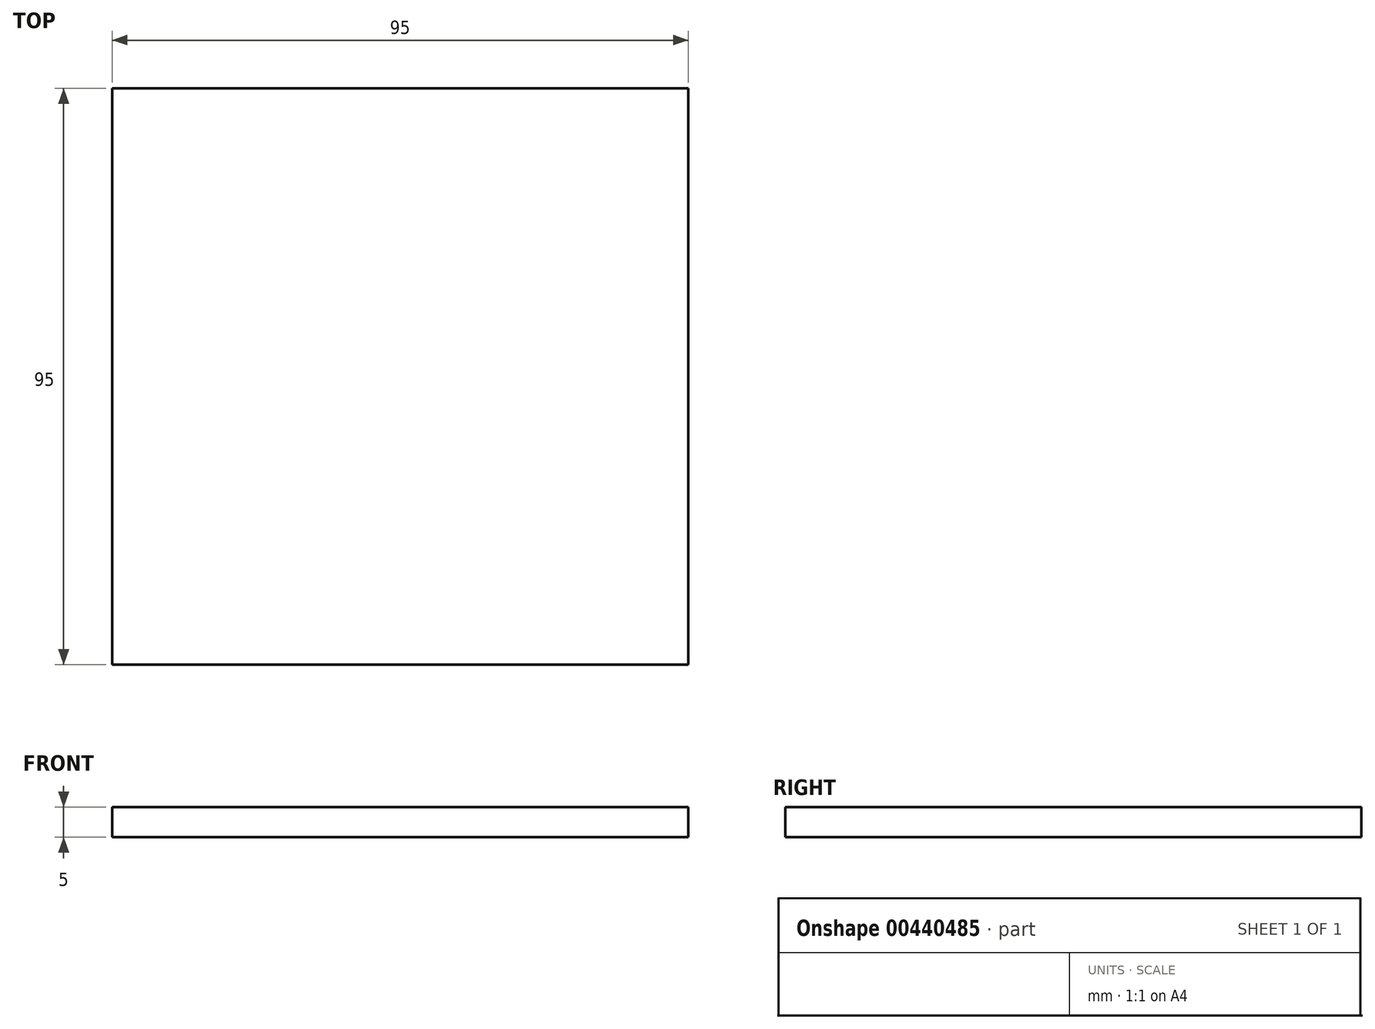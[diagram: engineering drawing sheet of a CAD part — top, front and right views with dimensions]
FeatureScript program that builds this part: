
annotation { "Feature Type Name" : "Feature", "Feature Type Description" : "" }
export const myFeature = defineFeature(function(context is Context, id is Id, definition is map)
    precondition{}
    {
        {
            var Q0;
            Q0=qCreatedBy(makeId("Top.planeOp"),FACE);
            var sketch = newSketch(context, id + "F0", { "sketchPlane" : qUnion([Q0])});
            skLineSegment(sketch, "E0.bottom", {"start": v(-47.5, -47.5) * mm, "end": v(47.5, -47.5) * mm});
            skLineSegment(sketch, "E0.top", {"start": v(-47.5, 47.5) * mm, "end": v(47.5, 47.5) * mm});
            skLineSegment(sketch, "E0.left", {"start": v(-47.5, -47.5) * mm, "end": v(-47.5, 47.5) * mm});
            skLineSegment(sketch, "E0.right", {"start": v(47.5, -47.5) * mm, "end": v(47.5, 47.5) * mm});
            skPoint(sketch, "E0.middle", {"position": v(0, 0) * mm});
            skSolve(sketch);
        }
        {
            var Q0;
            Q0 = qSketchRegion(id + "F0", true);
            extrude(context, id + "F1", {"entities" : qUnion([Q0]), "depth" : 5 * mm, "offsetDistance" : 25 * mm});
        }
    });
